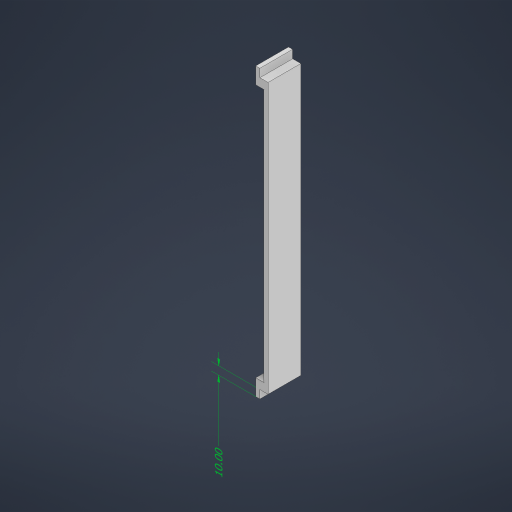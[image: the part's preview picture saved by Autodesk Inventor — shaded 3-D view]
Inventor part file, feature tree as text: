
AUTODESK INVENTOR PART (.ipt)
format: ipt  version: 2024 (Build 280153000, 153)  size: 210,944 bytes
history: native  units: mm
features: extrude x5, sketch x5, other x2
ambient origin geometry x8: Origin, YZ Plane, XZ Plane, XY Plane, X Axis, Y Axis, Z Axis, Center Point
bodies: Body1 (feature_tree)
feature tree (12):
  other  "솔리드1"
  extrude  "돌출1"  Depth=20.0mm
  extrude  "돌출2"  Depth=40.0mm
  extrude  "돌출3"  Depth=5.0mm TaperAngle=0.0deg
  extrude  "돌출4"  Depth=40.0mm
  extrude  "돌출5"  Depth=10.0mm
  sketch  "스케치1"
  sketch  "스케치2"
  sketch  "스케치3"
  sketch  "스케치4"
  sketch  "스케치5"
  other  "선형 치수 1"
